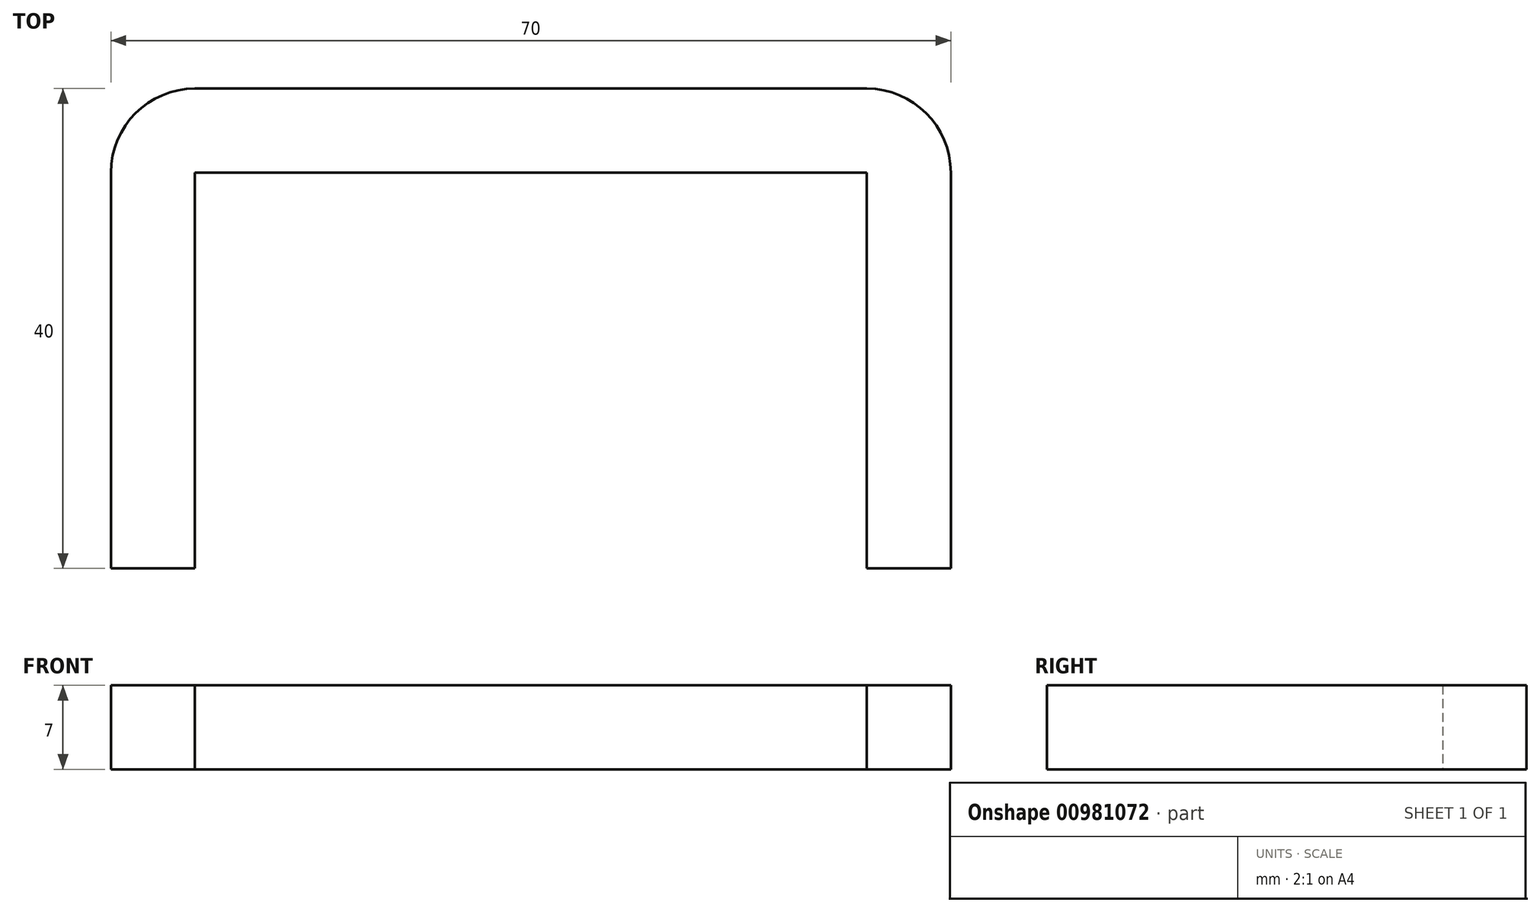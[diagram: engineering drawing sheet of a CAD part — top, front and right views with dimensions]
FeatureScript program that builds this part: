
annotation { "Feature Type Name" : "Feature", "Feature Type Description" : "" }
export const myFeature = defineFeature(function(context is Context, id is Id, definition is map)
    precondition{}
    {
        {
            var Q0;
            Q0=qCreatedBy(makeId("Top.planeOp"),FACE);
            var sketch = newSketch(context, id + "F0", { "sketchPlane" : qUnion([Q0])});
            skLineSegment(sketch, "E0.bottom", {"start": v(-63.5, 12.39) * mm, "end": v(-56.5, 12.39) * mm});
            skLineSegment(sketch, "E0.top", {"start": v(-56.5, 52.39) * mm, "end": v(-0.5, 52.39) * mm});
            skLineSegment(sketch, "E0.left", {"start": v(-63.5, 12.39) * mm, "end": v(-63.5, 45.39) * mm});
            skLineSegment(sketch, "E0.right", {"start": v(6.5, 12.39) * mm, "end": v(6.5, 45.39) * mm});
            skPoint(sketch, "E1.visualSharp", {"position": v(-63.5, 52.39) * mm});
            skArc(sketch, "E1.filletArc", {"start": v(-56.5, 52.39) * mm, "mid": v(-61.46, 50.34) * mm, "end": v(-63.5, 45.39) * mm});
            skPoint(sketch, "E2.visualSharp", {"position": v(6.5, 52.39) * mm});
            skArc(sketch, "E2.filletArc", {"start": v(6.5, 45.39) * mm, "mid": v(4.44, 50.34) * mm, "end": v(-0.5, 52.39) * mm});
            skLineSegment(sketch, "E3.top", {"start": v(-56.5, 45.39) * mm, "end": v(-0.5, 45.39) * mm});
            skLineSegment(sketch, "E3.left", {"start": v(-56.5, 12.39) * mm, "end": v(-56.5, 45.39) * mm});
            skLineSegment(sketch, "E3.right", {"start": v(-0.5, 12.39) * mm, "end": v(-0.5, 45.39) * mm});
            skLineSegment(sketch, "E4.trimOffspring", {"start": v(-0.5, 12.39) * mm, "end": v(6.5, 12.39) * mm});
            skSolve(sketch);
        }
        {
            var Q0;
            Q0 = qSketchRegion(id + "F0", true);
            extrude(context, id + "F1", {"entities" : qUnion([Q0]), "depth" : 7 * mm, "offsetDistance" : 25 * mm});
        }
    });
